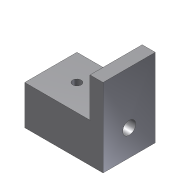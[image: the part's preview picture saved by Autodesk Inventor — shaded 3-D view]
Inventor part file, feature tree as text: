
AUTODESK INVENTOR PART (.ipt)
format: ipt  version: 2012 (Build 160160000, 160)  size: 105,984 bytes
history: native  units: in
note: dims shown in document units (in); Inventor stores cm internally (conversion verified against a paired STEP export)
features: extrude x4, sketch x4
ambient origin geometry x8: Origin, YZ Plane, XZ Plane, XY Plane, X Axis, Y Axis, Z Axis, Center Point
bodies: Solid1 (feature_tree)
feature tree (8):
  extrude  "Extrusion1"  Depth=1.5in
  extrude  "Extrusion2"  Depth=0.5in
  extrude  "Extrusion3"  Depth=1.0in TaperAngle=0.0deg
  extrude  "Extrusion5"  Depth=1.0in TaperAngle=0.0deg
  sketch  "Sketch1"  dims[d0=1.5in d1=1.5in]
  sketch  "Sketch2"  dims[d2=1.0in d3=0.0in d5=0.5in]
  sketch  "Sketch3"  dims[d6=0.25in d7=1.0in d8=0.0in]
  sketch  "Sketch5"  dims[d10=0.75in d11=1.0in d12=0.0in d18=0.5in d19=0.25in d20=0.5in d21=0.5in d22=1.0in d23=0.0in]
